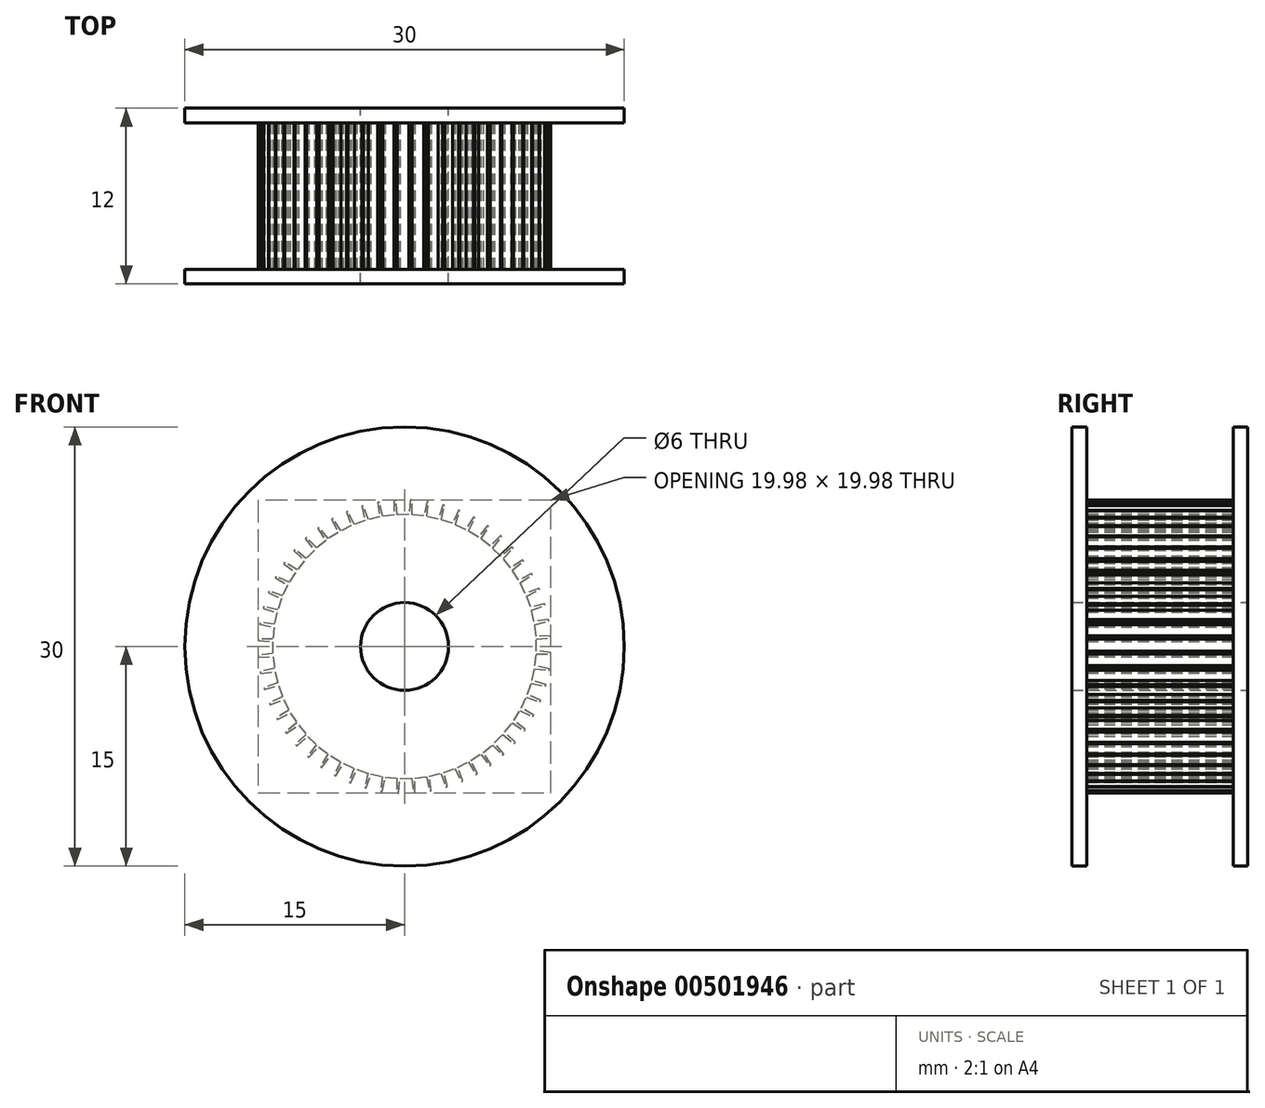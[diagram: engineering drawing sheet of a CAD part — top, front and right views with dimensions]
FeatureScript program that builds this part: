
annotation { "Feature Type Name" : "Feature", "Feature Type Description" : "" }
export const myFeature = defineFeature(function(context is Context, id is Id, definition is map)
    precondition{}
    {
        {
            var Q0;
            Q0=qCreatedBy(makeId("Right.planeOp"),FACE);
            var sketch = newSketch(context, id + "F0", { "sketchPlane" : qUnion([Q0])});
            skLineSegment(sketch, "E0.bottom", {"start": v(6, -7.5) * mm, "end": v(-6, -7.5) * mm});
            skLineSegment(sketch, "E0.top", {"start": v(6, 7.5) * mm, "end": v(5, 7.5) * mm});
            skLineSegment(sketch, "E0.left", {"start": v(6, -7.5) * mm, "end": v(6, 7.5) * mm});
            skLineSegment(sketch, "E0.right", {"start": v(-6, -7.5) * mm, "end": v(-6, 7.5) * mm});
            skPoint(sketch, "E0.middle", {"position": v(0, 0) * mm});
            skLineSegment(sketch, "E1.top", {"start": v(-5, 2.5) * mm, "end": v(5, 2.5) * mm});
            skLineSegment(sketch, "E1.left", {"start": v(-5, 7.5) * mm, "end": v(-5, 2.5) * mm});
            skLineSegment(sketch, "E1.right", {"start": v(5, 7.5) * mm, "end": v(5, 2.5) * mm});
            skLineSegment(sketch, "E2.trimOffspring", {"start": v(-5, 7.5) * mm, "end": v(-6, 7.5) * mm});
            skSolve(sketch);
        }
        {
            var Q0;
            Q0=makeQuery(id+"F0.imprint","IMPRINT",FACE,{"disambiguationData":[TD([[makeQuery(id+"F0.imprint","IMPRINT",EDGE,{"derivedFrom":sQuery(id+"F0.wireOp",EDGE,"E0.bottom")}),-1.0]])]});
            var Q1;
            Q1=sQuery(id+"F0.wireOp",EDGE,"E0.bottom");
            revolve(context, id + "F1", {"entities" : qUnion([Q0]), "axis" : qUnion([Q1]), "revolveType" : RevolveType.FULL});
        }
        {
            var Q0;
            Q0=makeQuery(id+"F1.opRevolve","SWEPT_FACE",FACE,{"disambiguationData":[OSD([sQuery(id+"F0.wireOp",EDGE,"E1.left")])]});
            var sketch = newSketch(context, id + "F2", { "sketchPlane" : qUnion([Q0])});
            skLineSegment(sketch, "E3", {"start": v(9.97, -8.22) * mm, "end": v(8.98, -8.2) * mm});
            skLineSegment(sketch, "E4", {"start": v(8.98, -8.2) * mm, "end": v(8.88, -9) * mm});
            skLineSegment(sketch, "E5", {"start": v(8.88, -9) * mm, "end": v(9.85, -9.22) * mm});
            skArc(sketch, "E6", {"start": v(9.85, -9.22) * mm, "mid": v(9.93, -8.72) * mm, "end": v(9.97, -8.22) * mm});
            skArc(sketch, "E7.1.0", {"start": v(9.98, -8.1) * mm, "mid": v(10, -7.6) * mm, "end": v(10, -7.1) * mm});
            skLineSegment(sketch, "E7.1.1", {"start": v(10, -7.1) * mm, "end": v(9, -7.2) * mm});
            skLineSegment(sketch, "E7.1.2", {"start": v(9, -8) * mm, "end": v(9.98, -8.1) * mm});
            skLineSegment(sketch, "E7.1.3", {"start": v(9, -7.2) * mm, "end": v(9, -8) * mm});
            skArc(sketch, "E7.2.0", {"start": v(9.99, -6.98) * mm, "mid": v(9.95, -6.48) * mm, "end": v(9.88, -5.98) * mm});
            skLineSegment(sketch, "E7.2.1", {"start": v(9.88, -5.98) * mm, "end": v(8.91, -6.19) * mm});
            skLineSegment(sketch, "E7.2.2", {"start": v(9, -6.98) * mm, "end": v(9.99, -6.98) * mm});
            skLineSegment(sketch, "E7.2.3", {"start": v(8.91, -6.19) * mm, "end": v(9, -6.98) * mm});
            skArc(sketch, "E7.3.0", {"start": v(9.87, -5.87) * mm, "mid": v(9.77, -5.37) * mm, "end": v(9.65, -4.88) * mm});
            skLineSegment(sketch, "E7.3.1", {"start": v(9.65, -4.88) * mm, "end": v(8.7, -5.2) * mm});
            skLineSegment(sketch, "E7.3.2", {"start": v(8.88, -5.98) * mm, "end": v(9.87, -5.87) * mm});
            skLineSegment(sketch, "E7.3.3", {"start": v(8.7, -5.2) * mm, "end": v(8.88, -5.98) * mm});
            skArc(sketch, "E7.4.0", {"start": v(9.62, -4.78) * mm, "mid": v(9.47, -4.3) * mm, "end": v(9.3, -3.82) * mm});
            skLineSegment(sketch, "E7.4.1", {"start": v(9.3, -3.82) * mm, "end": v(8.4, -4.24) * mm});
            skLineSegment(sketch, "E7.4.2", {"start": v(8.65, -5) * mm, "end": v(9.62, -4.78) * mm});
            skLineSegment(sketch, "E7.4.3", {"start": v(8.4, -4.24) * mm, "end": v(8.65, -5) * mm});
            skArc(sketch, "E7.5.0", {"start": v(9.26, -3.71) * mm, "mid": v(9.05, -3.25) * mm, "end": v(8.83, -2.8) * mm});
            skLineSegment(sketch, "E7.5.1", {"start": v(8.83, -2.8) * mm, "end": v(7.98, -3.32) * mm});
            skLineSegment(sketch, "E7.5.2", {"start": v(8.32, -4.04) * mm, "end": v(9.26, -3.71) * mm});
            skLineSegment(sketch, "E7.5.3", {"start": v(7.98, -3.32) * mm, "end": v(8.32, -4.04) * mm});
            skArc(sketch, "E7.6.0", {"start": v(8.77, -2.7) * mm, "mid": v(8.52, -2.27) * mm, "end": v(8.25, -1.84) * mm});
            skLineSegment(sketch, "E7.6.1", {"start": v(8.25, -1.84) * mm, "end": v(7.46, -2.45) * mm});
            skLineSegment(sketch, "E7.6.2", {"start": v(7.88, -3.13) * mm, "end": v(8.77, -2.7) * mm});
            skLineSegment(sketch, "E7.6.3", {"start": v(7.46, -2.45) * mm, "end": v(7.88, -3.13) * mm});
            skArc(sketch, "E7.7.0", {"start": v(8.18, -1.75) * mm, "mid": v(7.88, -1.35) * mm, "end": v(7.56, -0.96) * mm});
            skLineSegment(sketch, "E7.7.1", {"start": v(7.56, -0.96) * mm, "end": v(6.85, -1.65) * mm});
            skLineSegment(sketch, "E7.7.2", {"start": v(7.34, -2.28) * mm, "end": v(8.18, -1.75) * mm});
            skLineSegment(sketch, "E7.7.3", {"start": v(6.85, -1.65) * mm, "end": v(7.34, -2.28) * mm});
            skArc(sketch, "E7.8.0", {"start": v(7.49, -0.87) * mm, "mid": v(7.14, -0.5) * mm, "end": v(6.78, -0.15) * mm});
            skLineSegment(sketch, "E7.8.1", {"start": v(6.78, -0.15) * mm, "end": v(6.15, -0.92) * mm});
            skLineSegment(sketch, "E7.8.2", {"start": v(6.7, -1.49) * mm, "end": v(7.49, -0.87) * mm});
            skLineSegment(sketch, "E7.8.3", {"start": v(6.15, -0.92) * mm, "end": v(6.7, -1.49) * mm});
            skArc(sketch, "E7.9.0", {"start": v(6.7, -0.07) * mm, "mid": v(6.31, 0.25) * mm, "end": v(5.92, 0.56) * mm});
            skLineSegment(sketch, "E7.9.1", {"start": v(5.92, 0.56) * mm, "end": v(5.37, -0.27) * mm});
            skLineSegment(sketch, "E7.9.2", {"start": v(6, -0.77) * mm, "end": v(6.7, -0.07) * mm});
            skLineSegment(sketch, "E7.9.3", {"start": v(5.37, -0.27) * mm, "end": v(6, -0.77) * mm});
            skArc(sketch, "E7.10.0", {"start": v(5.82, 0.63) * mm, "mid": v(5.4, 0.91) * mm, "end": v(4.98, 1.17) * mm});
            skLineSegment(sketch, "E7.10.1", {"start": v(4.98, 1.17) * mm, "end": v(4.53, 0.29) * mm});
            skLineSegment(sketch, "E7.10.2", {"start": v(5.2, -0.15) * mm, "end": v(5.82, 0.63) * mm});
            skLineSegment(sketch, "E7.10.3", {"start": v(4.53, 0.29) * mm, "end": v(5.2, -0.15) * mm});
            skArc(sketch, "E7.11.0", {"start": v(4.88, 1.23) * mm, "mid": v(4.43, 1.46) * mm, "end": v(3.97, 1.68) * mm});
            skLineSegment(sketch, "E7.11.1", {"start": v(3.97, 1.68) * mm, "end": v(3.63, 0.75) * mm});
            skLineSegment(sketch, "E7.11.2", {"start": v(4.35, 0.4) * mm, "end": v(4.88, 1.23) * mm});
            skLineSegment(sketch, "E7.11.3", {"start": v(3.63, 0.75) * mm, "end": v(4.35, 0.4) * mm});
            skArc(sketch, "E7.12.0", {"start": v(3.87, 1.72) * mm, "mid": v(3.4, 1.9) * mm, "end": v(2.92, 2.06) * mm});
            skLineSegment(sketch, "E7.12.1", {"start": v(2.92, 2.06) * mm, "end": v(2.68, 1.1) * mm});
            skLineSegment(sketch, "E7.12.2", {"start": v(3.44, 0.83) * mm, "end": v(3.87, 1.72) * mm});
            skLineSegment(sketch, "E7.12.3", {"start": v(2.68, 1.1) * mm, "end": v(3.44, 0.83) * mm});
            skArc(sketch, "E7.13.0", {"start": v(2.81, 2.1) * mm, "mid": v(2.32, 2.23) * mm, "end": v(1.83, 2.33) * mm});
            skLineSegment(sketch, "E7.13.1", {"start": v(1.83, 2.33) * mm, "end": v(1.7, 1.35) * mm});
            skLineSegment(sketch, "E7.13.2", {"start": v(2.48, 1.16) * mm, "end": v(2.81, 2.1) * mm});
            skLineSegment(sketch, "E7.13.3", {"start": v(1.7, 1.35) * mm, "end": v(2.48, 1.16) * mm});
            skArc(sketch, "E7.14.0", {"start": v(1.72, 2.35) * mm, "mid": v(1.22, 2.43) * mm, "end": v(0.72, 2.47) * mm});
            skLineSegment(sketch, "E7.14.1", {"start": v(0.72, 2.47) * mm, "end": v(0.7, 1.48) * mm});
            skLineSegment(sketch, "E7.14.2", {"start": v(1.5, 1.38) * mm, "end": v(1.72, 2.35) * mm});
            skLineSegment(sketch, "E7.14.3", {"start": v(0.7, 1.48) * mm, "end": v(1.5, 1.38) * mm});
            skArc(sketch, "E7.15.0", {"start": v(0.6, 2.48) * mm, "mid": v(0.1, 2.5) * mm, "end": v(-0.4, 2.5) * mm});
            skLineSegment(sketch, "E7.15.1", {"start": v(-0.4, 2.5) * mm, "end": v(-0.3, 1.5) * mm});
            skLineSegment(sketch, "E7.15.2", {"start": v(0.5, 1.5) * mm, "end": v(0.6, 2.48) * mm});
            skLineSegment(sketch, "E7.15.3", {"start": v(-0.3, 1.5) * mm, "end": v(0.5, 1.5) * mm});
            skArc(sketch, "E7.16.0", {"start": v(-0.52, 2.49) * mm, "mid": v(-1.02, 2.45) * mm, "end": v(-1.52, 2.38) * mm});
            skLineSegment(sketch, "E7.16.1", {"start": v(-1.52, 2.38) * mm, "end": v(-1.31, 1.41) * mm});
            skLineSegment(sketch, "E7.16.2", {"start": v(-0.52, 1.5) * mm, "end": v(-0.52, 2.49) * mm});
            skLineSegment(sketch, "E7.16.3", {"start": v(-1.31, 1.41) * mm, "end": v(-0.52, 1.5) * mm});
            skArc(sketch, "E7.17.0", {"start": v(-1.63, 2.37) * mm, "mid": v(-2.13, 2.27) * mm, "end": v(-2.62, 2.15) * mm});
            skLineSegment(sketch, "E7.17.1", {"start": v(-2.62, 2.15) * mm, "end": v(-2.3, 1.2) * mm});
            skLineSegment(sketch, "E7.17.2", {"start": v(-1.52, 1.38) * mm, "end": v(-1.63, 2.37) * mm});
            skLineSegment(sketch, "E7.17.3", {"start": v(-2.3, 1.2) * mm, "end": v(-1.52, 1.38) * mm});
            skArc(sketch, "E7.18.0", {"start": v(-2.72, 2.12) * mm, "mid": v(-3.2, 1.97) * mm, "end": v(-3.68, 1.8) * mm});
            skLineSegment(sketch, "E7.18.1", {"start": v(-3.68, 1.8) * mm, "end": v(-3.26, 0.9) * mm});
            skLineSegment(sketch, "E7.18.2", {"start": v(-2.5, 1.15) * mm, "end": v(-2.72, 2.12) * mm});
            skLineSegment(sketch, "E7.18.3", {"start": v(-3.26, 0.9) * mm, "end": v(-2.5, 1.15) * mm});
            skArc(sketch, "E7.19.0", {"start": v(-3.79, 1.76) * mm, "mid": v(-4.25, 1.55) * mm, "end": v(-4.7, 1.33) * mm});
            skLineSegment(sketch, "E7.19.1", {"start": v(-4.7, 1.33) * mm, "end": v(-4.18, 0.48) * mm});
            skLineSegment(sketch, "E7.19.2", {"start": v(-3.46, 0.82) * mm, "end": v(-3.79, 1.76) * mm});
            skLineSegment(sketch, "E7.19.3", {"start": v(-4.18, 0.48) * mm, "end": v(-3.46, 0.82) * mm});
            skArc(sketch, "E7.20.0", {"start": v(-4.8, 1.27) * mm, "mid": v(-5.23, 1.02) * mm, "end": v(-5.66, 0.75) * mm});
            skLineSegment(sketch, "E7.20.1", {"start": v(-5.66, 0.75) * mm, "end": v(-5.05, -0.04) * mm});
            skLineSegment(sketch, "E7.20.2", {"start": v(-4.37, 0.38) * mm, "end": v(-4.8, 1.27) * mm});
            skLineSegment(sketch, "E7.20.3", {"start": v(-5.05, -0.04) * mm, "end": v(-4.37, 0.38) * mm});
            skArc(sketch, "E7.21.0", {"start": v(-5.75, 0.68) * mm, "mid": v(-6.15, 0.38) * mm, "end": v(-6.54, 0.06) * mm});
            skLineSegment(sketch, "E7.21.1", {"start": v(-6.54, 0.06) * mm, "end": v(-5.85, -0.65) * mm});
            skLineSegment(sketch, "E7.21.2", {"start": v(-5.22, -0.16) * mm, "end": v(-5.75, 0.68) * mm});
            skLineSegment(sketch, "E7.21.3", {"start": v(-5.85, -0.65) * mm, "end": v(-5.22, -0.16) * mm});
            skArc(sketch, "E7.22.0", {"start": v(-6.63, -0.01) * mm, "mid": v(-7, -0.36) * mm, "end": v(-7.35, -0.72) * mm});
            skLineSegment(sketch, "E7.22.1", {"start": v(-7.35, -0.72) * mm, "end": v(-6.58, -1.35) * mm});
            skLineSegment(sketch, "E7.22.2", {"start": v(-6.01, -0.8) * mm, "end": v(-6.63, -0.01) * mm});
            skLineSegment(sketch, "E7.22.3", {"start": v(-6.58, -1.35) * mm, "end": v(-6.01, -0.8) * mm});
            skArc(sketch, "E7.23.0", {"start": v(-7.43, -0.8) * mm, "mid": v(-7.75, -1.19) * mm, "end": v(-8.06, -1.58) * mm});
            skLineSegment(sketch, "E7.23.1", {"start": v(-8.06, -1.58) * mm, "end": v(-7.23, -2.13) * mm});
            skLineSegment(sketch, "E7.23.2", {"start": v(-6.73, -1.5) * mm, "end": v(-7.43, -0.8) * mm});
            skLineSegment(sketch, "E7.23.3", {"start": v(-7.23, -2.13) * mm, "end": v(-6.73, -1.5) * mm});
            skArc(sketch, "E7.24.0", {"start": v(-8.13, -1.68) * mm, "mid": v(-8.41, -2.1) * mm, "end": v(-8.67, -2.52) * mm});
            skLineSegment(sketch, "E7.24.1", {"start": v(-8.67, -2.52) * mm, "end": v(-7.79, -2.97) * mm});
            skLineSegment(sketch, "E7.24.2", {"start": v(-7.35, -2.3) * mm, "end": v(-8.13, -1.68) * mm});
            skLineSegment(sketch, "E7.24.3", {"start": v(-7.79, -2.97) * mm, "end": v(-7.35, -2.3) * mm});
            skArc(sketch, "E7.25.0", {"start": v(-8.73, -2.62) * mm, "mid": v(-8.96, -3.07) * mm, "end": v(-9.18, -3.53) * mm});
            skLineSegment(sketch, "E7.25.1", {"start": v(-9.18, -3.53) * mm, "end": v(-8.25, -3.87) * mm});
            skLineSegment(sketch, "E7.25.2", {"start": v(-7.9, -3.15) * mm, "end": v(-8.73, -2.62) * mm});
            skLineSegment(sketch, "E7.25.3", {"start": v(-8.25, -3.87) * mm, "end": v(-7.9, -3.15) * mm});
            skArc(sketch, "E7.26.0", {"start": v(-9.22, -3.63) * mm, "mid": v(-9.4, -4.1) * mm, "end": v(-9.56, -4.58) * mm});
            skLineSegment(sketch, "E7.26.1", {"start": v(-9.56, -4.58) * mm, "end": v(-8.6, -4.82) * mm});
            skLineSegment(sketch, "E7.26.2", {"start": v(-8.33, -4.06) * mm, "end": v(-9.22, -3.63) * mm});
            skLineSegment(sketch, "E7.26.3", {"start": v(-8.6, -4.82) * mm, "end": v(-8.33, -4.06) * mm});
            skArc(sketch, "E7.27.0", {"start": v(-9.6, -4.69) * mm, "mid": v(-9.73, -5.18) * mm, "end": v(-9.83, -5.67) * mm});
            skLineSegment(sketch, "E7.27.1", {"start": v(-9.83, -5.67) * mm, "end": v(-8.85, -5.8) * mm});
            skLineSegment(sketch, "E7.27.2", {"start": v(-8.66, -5.02) * mm, "end": v(-9.6, -4.69) * mm});
            skLineSegment(sketch, "E7.27.3", {"start": v(-8.85, -5.8) * mm, "end": v(-8.66, -5.02) * mm});
            skArc(sketch, "E7.28.0", {"start": v(-9.85, -5.78) * mm, "mid": v(-9.93, -6.28) * mm, "end": v(-9.97, -6.78) * mm});
            skLineSegment(sketch, "E7.28.1", {"start": v(-9.97, -6.78) * mm, "end": v(-8.98, -6.8) * mm});
            skLineSegment(sketch, "E7.28.2", {"start": v(-8.88, -6) * mm, "end": v(-9.85, -5.78) * mm});
            skLineSegment(sketch, "E7.28.3", {"start": v(-8.98, -6.8) * mm, "end": v(-8.88, -6) * mm});
            skArc(sketch, "E7.29.0", {"start": v(-9.98, -6.9) * mm, "mid": v(-10, -7.4) * mm, "end": v(-10, -7.9) * mm});
            skLineSegment(sketch, "E7.29.1", {"start": v(-10, -7.9) * mm, "end": v(-9, -7.8) * mm});
            skLineSegment(sketch, "E7.29.2", {"start": v(-9, -7) * mm, "end": v(-9.98, -6.9) * mm});
            skLineSegment(sketch, "E7.29.3", {"start": v(-9, -7.8) * mm, "end": v(-9, -7) * mm});
            skArc(sketch, "E7.30.0", {"start": v(-9.99, -8.02) * mm, "mid": v(-9.95, -8.52) * mm, "end": v(-9.88, -9.02) * mm});
            skLineSegment(sketch, "E7.30.1", {"start": v(-9.88, -9.02) * mm, "end": v(-8.91, -8.81) * mm});
            skLineSegment(sketch, "E7.30.2", {"start": v(-9, -8.02) * mm, "end": v(-9.99, -8.02) * mm});
            skLineSegment(sketch, "E7.30.3", {"start": v(-8.91, -8.81) * mm, "end": v(-9, -8.02) * mm});
            skArc(sketch, "E7.31.0", {"start": v(-9.87, -9.13) * mm, "mid": v(-9.77, -9.63) * mm, "end": v(-9.65, -10.12) * mm});
            skLineSegment(sketch, "E7.31.1", {"start": v(-9.65, -10.12) * mm, "end": v(-8.7, -9.8) * mm});
            skLineSegment(sketch, "E7.31.2", {"start": v(-8.88, -9.02) * mm, "end": v(-9.87, -9.13) * mm});
            skLineSegment(sketch, "E7.31.3", {"start": v(-8.7, -9.8) * mm, "end": v(-8.88, -9.02) * mm});
            skArc(sketch, "E7.32.0", {"start": v(-9.62, -10.22) * mm, "mid": v(-9.47, -10.7) * mm, "end": v(-9.3, -11.18) * mm});
            skLineSegment(sketch, "E7.32.1", {"start": v(-9.3, -11.18) * mm, "end": v(-8.4, -10.76) * mm});
            skLineSegment(sketch, "E7.32.2", {"start": v(-8.65, -10) * mm, "end": v(-9.62, -10.22) * mm});
            skLineSegment(sketch, "E7.32.3", {"start": v(-8.4, -10.76) * mm, "end": v(-8.65, -10) * mm});
            skArc(sketch, "E7.33.0", {"start": v(-9.26, -11.29) * mm, "mid": v(-9.05, -11.75) * mm, "end": v(-8.83, -12.2) * mm});
            skLineSegment(sketch, "E7.33.1", {"start": v(-8.83, -12.2) * mm, "end": v(-7.98, -11.68) * mm});
            skLineSegment(sketch, "E7.33.2", {"start": v(-8.32, -10.96) * mm, "end": v(-9.26, -11.29) * mm});
            skLineSegment(sketch, "E7.33.3", {"start": v(-7.98, -11.68) * mm, "end": v(-8.32, -10.96) * mm});
            skArc(sketch, "E7.34.0", {"start": v(-8.77, -12.3) * mm, "mid": v(-8.52, -12.73) * mm, "end": v(-8.25, -13.16) * mm});
            skLineSegment(sketch, "E7.34.1", {"start": v(-8.25, -13.16) * mm, "end": v(-7.46, -12.55) * mm});
            skLineSegment(sketch, "E7.34.2", {"start": v(-7.88, -11.87) * mm, "end": v(-8.77, -12.3) * mm});
            skLineSegment(sketch, "E7.34.3", {"start": v(-7.46, -12.55) * mm, "end": v(-7.88, -11.87) * mm});
            skArc(sketch, "E7.35.0", {"start": v(-8.18, -13.25) * mm, "mid": v(-7.88, -13.65) * mm, "end": v(-7.56, -14.04) * mm});
            skLineSegment(sketch, "E7.35.1", {"start": v(-7.56, -14.04) * mm, "end": v(-6.85, -13.35) * mm});
            skLineSegment(sketch, "E7.35.2", {"start": v(-7.34, -12.72) * mm, "end": v(-8.18, -13.25) * mm});
            skLineSegment(sketch, "E7.35.3", {"start": v(-6.85, -13.35) * mm, "end": v(-7.34, -12.72) * mm});
            skArc(sketch, "E7.36.0", {"start": v(-7.49, -14.13) * mm, "mid": v(-7.14, -14.5) * mm, "end": v(-6.78, -14.85) * mm});
            skLineSegment(sketch, "E7.36.1", {"start": v(-6.78, -14.85) * mm, "end": v(-6.15, -14.08) * mm});
            skLineSegment(sketch, "E7.36.2", {"start": v(-6.7, -13.51) * mm, "end": v(-7.49, -14.13) * mm});
            skLineSegment(sketch, "E7.36.3", {"start": v(-6.15, -14.08) * mm, "end": v(-6.7, -13.51) * mm});
            skArc(sketch, "E7.37.0", {"start": v(-6.7, -14.93) * mm, "mid": v(-6.31, -15.25) * mm, "end": v(-5.92, -15.56) * mm});
            skLineSegment(sketch, "E7.37.1", {"start": v(-5.92, -15.56) * mm, "end": v(-5.37, -14.73) * mm});
            skLineSegment(sketch, "E7.37.2", {"start": v(-6, -14.23) * mm, "end": v(-6.7, -14.93) * mm});
            skLineSegment(sketch, "E7.37.3", {"start": v(-5.37, -14.73) * mm, "end": v(-6, -14.23) * mm});
            skArc(sketch, "E7.38.0", {"start": v(-5.82, -15.63) * mm, "mid": v(-5.4, -15.91) * mm, "end": v(-4.98, -16.17) * mm});
            skLineSegment(sketch, "E7.38.1", {"start": v(-4.98, -16.17) * mm, "end": v(-4.53, -15.29) * mm});
            skLineSegment(sketch, "E7.38.2", {"start": v(-5.2, -14.85) * mm, "end": v(-5.82, -15.63) * mm});
            skLineSegment(sketch, "E7.38.3", {"start": v(-4.53, -15.29) * mm, "end": v(-5.2, -14.85) * mm});
            skArc(sketch, "E7.39.0", {"start": v(-4.88, -16.23) * mm, "mid": v(-4.43, -16.46) * mm, "end": v(-3.97, -16.68) * mm});
            skLineSegment(sketch, "E7.39.1", {"start": v(-3.97, -16.68) * mm, "end": v(-3.63, -15.75) * mm});
            skLineSegment(sketch, "E7.39.2", {"start": v(-4.35, -15.4) * mm, "end": v(-4.88, -16.23) * mm});
            skLineSegment(sketch, "E7.39.3", {"start": v(-3.63, -15.75) * mm, "end": v(-4.35, -15.4) * mm});
            skArc(sketch, "E7.40.0", {"start": v(-3.87, -16.72) * mm, "mid": v(-3.4, -16.9) * mm, "end": v(-2.92, -17.06) * mm});
            skLineSegment(sketch, "E7.40.1", {"start": v(-2.92, -17.06) * mm, "end": v(-2.68, -16.1) * mm});
            skLineSegment(sketch, "E7.40.2", {"start": v(-3.44, -15.83) * mm, "end": v(-3.87, -16.72) * mm});
            skLineSegment(sketch, "E7.40.3", {"start": v(-2.68, -16.1) * mm, "end": v(-3.44, -15.83) * mm});
            skArc(sketch, "E7.41.0", {"start": v(-2.81, -17.1) * mm, "mid": v(-2.32, -17.23) * mm, "end": v(-1.83, -17.33) * mm});
            skLineSegment(sketch, "E7.41.1", {"start": v(-1.83, -17.33) * mm, "end": v(-1.7, -16.35) * mm});
            skLineSegment(sketch, "E7.41.2", {"start": v(-2.48, -16.16) * mm, "end": v(-2.81, -17.1) * mm});
            skLineSegment(sketch, "E7.41.3", {"start": v(-1.7, -16.35) * mm, "end": v(-2.48, -16.16) * mm});
            skArc(sketch, "E7.42.0", {"start": v(-1.72, -17.35) * mm, "mid": v(-1.22, -17.43) * mm, "end": v(-0.72, -17.47) * mm});
            skLineSegment(sketch, "E7.42.1", {"start": v(-0.72, -17.47) * mm, "end": v(-0.7, -16.48) * mm});
            skLineSegment(sketch, "E7.42.2", {"start": v(-1.5, -16.38) * mm, "end": v(-1.72, -17.35) * mm});
            skLineSegment(sketch, "E7.42.3", {"start": v(-0.7, -16.48) * mm, "end": v(-1.5, -16.38) * mm});
            skArc(sketch, "E7.43.0", {"start": v(-0.6, -17.48) * mm, "mid": v(-0.1, -17.5) * mm, "end": v(0.4, -17.5) * mm});
            skLineSegment(sketch, "E7.43.1", {"start": v(0.4, -17.5) * mm, "end": v(0.3, -16.5) * mm});
            skLineSegment(sketch, "E7.43.2", {"start": v(-0.5, -16.5) * mm, "end": v(-0.6, -17.48) * mm});
            skLineSegment(sketch, "E7.43.3", {"start": v(0.3, -16.5) * mm, "end": v(-0.5, -16.5) * mm});
            skArc(sketch, "E7.44.0", {"start": v(0.52, -17.49) * mm, "mid": v(1.02, -17.45) * mm, "end": v(1.52, -17.38) * mm});
            skLineSegment(sketch, "E7.44.1", {"start": v(1.52, -17.38) * mm, "end": v(1.31, -16.41) * mm});
            skLineSegment(sketch, "E7.44.2", {"start": v(0.52, -16.5) * mm, "end": v(0.52, -17.49) * mm});
            skLineSegment(sketch, "E7.44.3", {"start": v(1.31, -16.41) * mm, "end": v(0.52, -16.5) * mm});
            skArc(sketch, "E7.45.0", {"start": v(1.63, -17.37) * mm, "mid": v(2.13, -17.27) * mm, "end": v(2.62, -17.15) * mm});
            skLineSegment(sketch, "E7.45.1", {"start": v(2.62, -17.15) * mm, "end": v(2.3, -16.2) * mm});
            skLineSegment(sketch, "E7.45.2", {"start": v(1.52, -16.38) * mm, "end": v(1.63, -17.37) * mm});
            skLineSegment(sketch, "E7.45.3", {"start": v(2.3, -16.2) * mm, "end": v(1.52, -16.38) * mm});
            skArc(sketch, "E7.46.0", {"start": v(2.72, -17.12) * mm, "mid": v(3.2, -16.97) * mm, "end": v(3.68, -16.8) * mm});
            skLineSegment(sketch, "E7.46.1", {"start": v(3.68, -16.8) * mm, "end": v(3.26, -15.9) * mm});
            skLineSegment(sketch, "E7.46.2", {"start": v(2.5, -16.15) * mm, "end": v(2.72, -17.12) * mm});
            skLineSegment(sketch, "E7.46.3", {"start": v(3.26, -15.9) * mm, "end": v(2.5, -16.15) * mm});
            skArc(sketch, "E7.47.0", {"start": v(3.79, -16.76) * mm, "mid": v(4.25, -16.55) * mm, "end": v(4.7, -16.33) * mm});
            skLineSegment(sketch, "E7.47.1", {"start": v(4.7, -16.33) * mm, "end": v(4.18, -15.48) * mm});
            skLineSegment(sketch, "E7.47.2", {"start": v(3.46, -15.82) * mm, "end": v(3.79, -16.76) * mm});
            skLineSegment(sketch, "E7.47.3", {"start": v(4.18, -15.48) * mm, "end": v(3.46, -15.82) * mm});
            skArc(sketch, "E7.48.0", {"start": v(4.8, -16.27) * mm, "mid": v(5.23, -16.02) * mm, "end": v(5.66, -15.75) * mm});
            skLineSegment(sketch, "E7.48.1", {"start": v(5.66, -15.75) * mm, "end": v(5.05, -14.96) * mm});
            skLineSegment(sketch, "E7.48.2", {"start": v(4.37, -15.38) * mm, "end": v(4.8, -16.27) * mm});
            skLineSegment(sketch, "E7.48.3", {"start": v(5.05, -14.96) * mm, "end": v(4.37, -15.38) * mm});
            skArc(sketch, "E7.49.0", {"start": v(5.75, -15.68) * mm, "mid": v(6.15, -15.38) * mm, "end": v(6.54, -15.06) * mm});
            skLineSegment(sketch, "E7.49.1", {"start": v(6.54, -15.06) * mm, "end": v(5.85, -14.35) * mm});
            skLineSegment(sketch, "E7.49.2", {"start": v(5.22, -14.84) * mm, "end": v(5.75, -15.68) * mm});
            skLineSegment(sketch, "E7.49.3", {"start": v(5.85, -14.35) * mm, "end": v(5.22, -14.84) * mm});
            skArc(sketch, "E7.50.0", {"start": v(6.63, -14.99) * mm, "mid": v(7, -14.64) * mm, "end": v(7.35, -14.28) * mm});
            skLineSegment(sketch, "E7.50.1", {"start": v(7.35, -14.28) * mm, "end": v(6.58, -13.65) * mm});
            skLineSegment(sketch, "E7.50.2", {"start": v(6.01, -14.2) * mm, "end": v(6.63, -14.99) * mm});
            skLineSegment(sketch, "E7.50.3", {"start": v(6.58, -13.65) * mm, "end": v(6.01, -14.2) * mm});
            skArc(sketch, "E7.51.0", {"start": v(7.43, -14.2) * mm, "mid": v(7.75, -13.81) * mm, "end": v(8.06, -13.42) * mm});
            skLineSegment(sketch, "E7.51.1", {"start": v(8.06, -13.42) * mm, "end": v(7.23, -12.87) * mm});
            skLineSegment(sketch, "E7.51.2", {"start": v(6.73, -13.5) * mm, "end": v(7.43, -14.2) * mm});
            skLineSegment(sketch, "E7.51.3", {"start": v(7.23, -12.87) * mm, "end": v(6.73, -13.5) * mm});
            skArc(sketch, "E7.52.0", {"start": v(8.13, -13.32) * mm, "mid": v(8.41, -12.9) * mm, "end": v(8.67, -12.48) * mm});
            skLineSegment(sketch, "E7.52.1", {"start": v(8.67, -12.48) * mm, "end": v(7.79, -12.03) * mm});
            skLineSegment(sketch, "E7.52.2", {"start": v(7.35, -12.7) * mm, "end": v(8.13, -13.32) * mm});
            skLineSegment(sketch, "E7.52.3", {"start": v(7.79, -12.03) * mm, "end": v(7.35, -12.7) * mm});
            skArc(sketch, "E7.53.0", {"start": v(8.73, -12.38) * mm, "mid": v(8.96, -11.93) * mm, "end": v(9.18, -11.47) * mm});
            skLineSegment(sketch, "E7.53.1", {"start": v(9.18, -11.47) * mm, "end": v(8.25, -11.13) * mm});
            skLineSegment(sketch, "E7.53.2", {"start": v(7.9, -11.85) * mm, "end": v(8.73, -12.38) * mm});
            skLineSegment(sketch, "E7.53.3", {"start": v(8.25, -11.13) * mm, "end": v(7.9, -11.85) * mm});
            skArc(sketch, "E7.54.0", {"start": v(9.22, -11.37) * mm, "mid": v(9.4, -10.9) * mm, "end": v(9.56, -10.42) * mm});
            skLineSegment(sketch, "E7.54.1", {"start": v(9.56, -10.42) * mm, "end": v(8.6, -10.18) * mm});
            skLineSegment(sketch, "E7.54.2", {"start": v(8.33, -10.94) * mm, "end": v(9.22, -11.37) * mm});
            skLineSegment(sketch, "E7.54.3", {"start": v(8.6, -10.18) * mm, "end": v(8.33, -10.94) * mm});
            skArc(sketch, "E7.55.0", {"start": v(9.6, -10.31) * mm, "mid": v(9.73, -9.82) * mm, "end": v(9.83, -9.33) * mm});
            skLineSegment(sketch, "E7.55.1", {"start": v(9.83, -9.33) * mm, "end": v(8.85, -9.2) * mm});
            skLineSegment(sketch, "E7.55.2", {"start": v(8.66, -9.98) * mm, "end": v(9.6, -10.31) * mm});
            skLineSegment(sketch, "E7.55.3", {"start": v(8.85, -9.2) * mm, "end": v(8.66, -9.98) * mm});
            skSolve(sketch);
        }
        {
            var Q0;
            Q0 = qSketchRegion(id + "F2", true);
            extrude(context, id + "F3", {"entities" : qUnion([Q0]), "operationType" : NewBodyOperationType.REMOVE, "depth" : 10 * mm});
        }
        {
            var Q0;
            Q0=makeQuery(id+"F1.opRevolve","SWEPT_FACE",FACE,{"disambiguationData":[OSD([sQuery(id+"F0.wireOp",EDGE,"E0.left")])]});
            var sketch = newSketch(context, id + "F4", { "sketchPlane" : qUnion([Q0])});
            skCircle(sketch, "E8", {"center": v(0, -7.5) * mm, "radius": 3 * mm});
            skSolve(sketch);
        }
        {
            var Q0;
            Q0 = qSketchRegion(id + "F4", true);
            extrude(context, id + "F5", {"entities" : qUnion([Q0]), "operationType" : NewBodyOperationType.REMOVE, "oppositeDirection" : true, "depth" : 12 * mm});
        }
    });
